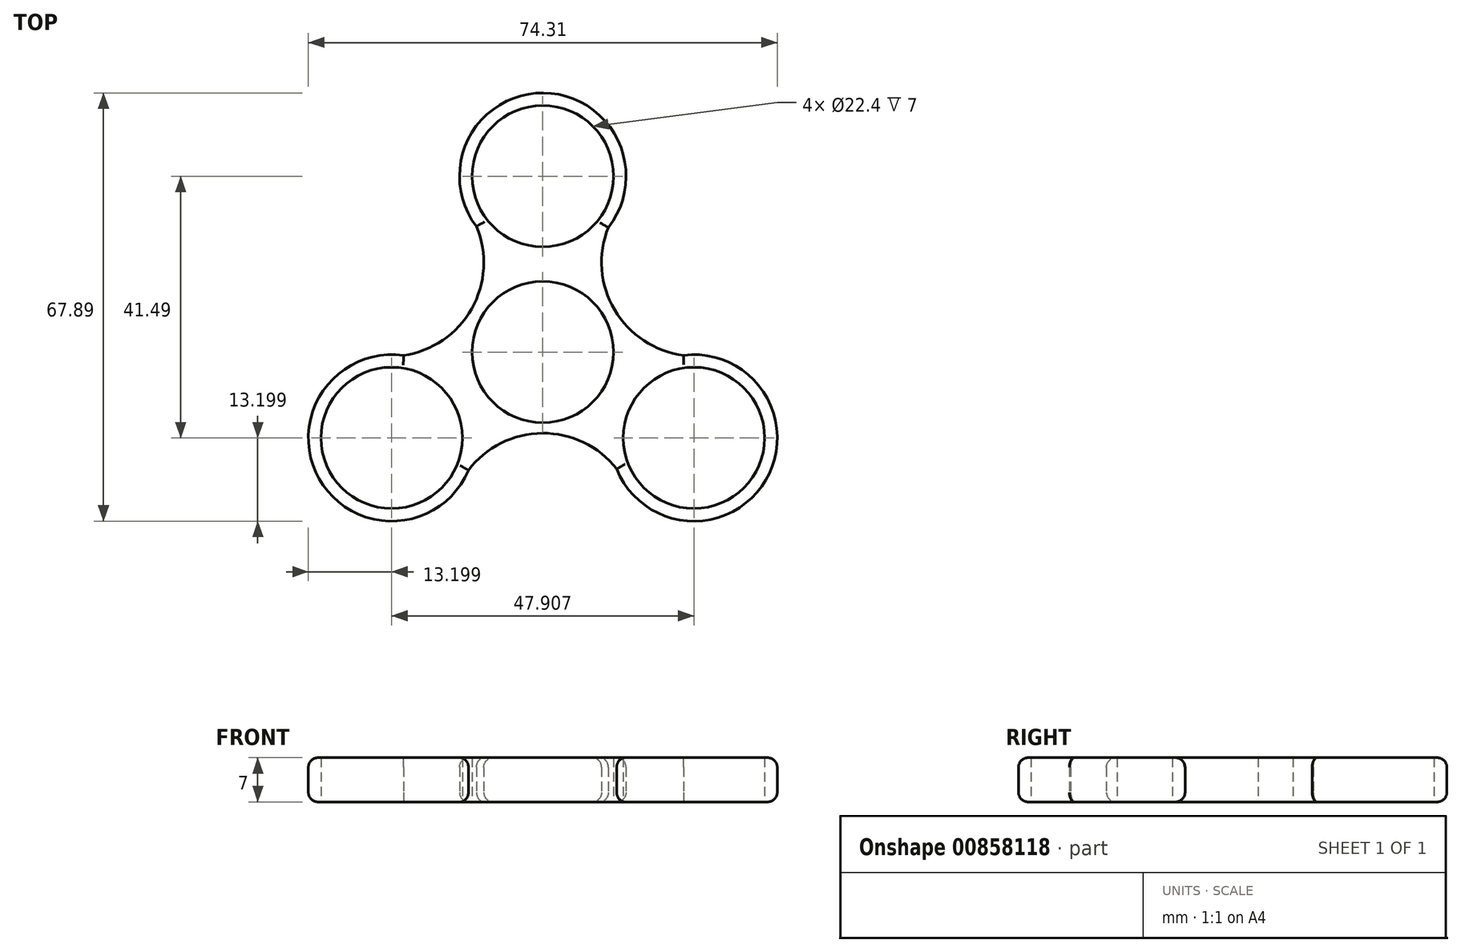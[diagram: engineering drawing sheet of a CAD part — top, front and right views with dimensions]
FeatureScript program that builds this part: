
annotation { "Feature Type Name" : "Feature", "Feature Type Description" : "" }
export const myFeature = defineFeature(function(context is Context, id is Id, definition is map)
    precondition{}
    {
        {
            var Q0;
            Q0=qCreatedBy(makeId("Top.planeOp"),FACE);
            var sketch = newSketch(context, id + "F0", { "sketchPlane" : qUnion([Q0])});
            skCircle(sketch, "E0", {"center": v(0, 0) * mm, "radius": 11.2 * mm});
            skArc(sketch, "E1", {"start": v(-2.14, -13.03) * mm, "mid": v(0.02, -13.2) * mm, "end": v(2.17, -13.02) * mm});
            skCircle(sketch, "E2", {"center": v(0, 27.88) * mm, "radius": 11.2 * mm});
            skArc(sketch, "E3", {"start": v(10.39, 19.74) * mm, "mid": v(0.1, 41.08) * mm, "end": v(-10.52, 19.9) * mm});
            skArc(sketch, "E4.1.0", {"start": v(-22.1, -0.54) * mm, "mid": v(-35.44, -20.12) * mm, "end": v(-11.79, -18.74) * mm});
            skCircle(sketch, "E4.1.1", {"center": v(-23.95, -13.61) * mm, "radius": 11.2 * mm});
            skArc(sketch, "E4.2.0", {"start": v(11.7, -18.53) * mm, "mid": v(35.33, -20.3) * mm, "end": v(22.31, -0.51) * mm});
            skCircle(sketch, "E4.2.1", {"center": v(23.96, -13.6) * mm, "radius": 11.2 * mm});
            skPoint(sketch, "E4.center", {"position": v(0, 0.22) * mm});
            skArc(sketch, "E5", {"start": v(10.39, 19.74) * mm, "mid": v(11.38, 6.68) * mm, "end": v(22.31, -0.51) * mm});
            skArc(sketch, "E6.1.0", {"start": v(-22.1, -0.54) * mm, "mid": v(-11.29, 6.84) * mm, "end": v(-10.52, 19.9) * mm});
            skArc(sketch, "E6.2.0", {"start": v(11.7, -18.53) * mm, "mid": v(-0.09, -12.87) * mm, "end": v(-11.79, -18.74) * mm});
            skArc(sketch, "E7.trimOffspring", {"start": v(-11.26, 6.89) * mm, "mid": v(-11.4, 6.66) * mm, "end": v(-11.53, 6.44) * mm});
            skLineSegment(sketch, "E8.trimOffspring", {"start": v(11.45, 6.57) * mm, "end": v(11.45, 6.57) * mm});
            skSolve(sketch);
        }
        {
            var Q0;
            Q0=makeQuery(id+"F0.imprint","IMPRINT",FACE,{"disambiguationData":[TD([[makeQuery(id+"F0.imprint","IMPRINT",EDGE,{"derivedFrom":sQuery(id+"F0.wireOp",EDGE,"E0")}),-1.0]])]});
            extrude(context, id + "F1", {"entities" : qUnion([Q0]), "depth" : 7 * mm, "offsetDistance" : 25 * mm});
        }
        {
            var Q0;
            Q0=makeQuery(id+"F1.opExtrude","CAP_EDGE",EDGE,{"disambiguationData":[OSD([sQuery(id+"F0.wireOp",EDGE,"E4.1.0")])],"isStart":false});
            var Q1;
            Q1=makeQuery(id+"F1.opExtrude","CAP_EDGE",EDGE,{"disambiguationData":[OSD([sQuery(id+"F0.wireOp",EDGE,"E6.1.0")])],"isStart":false});
            var Q2;
            Q2=makeQuery(id+"F1.opExtrude","CAP_EDGE",EDGE,{"disambiguationData":[OSD([sQuery(id+"F0.wireOp",EDGE,"E3")])],"isStart":false});
            var Q3;
            Q3=makeQuery(id+"F1.opExtrude","CAP_EDGE",EDGE,{"disambiguationData":[OSD([sQuery(id+"F0.wireOp",EDGE,"E6.2.0")])],"isStart":false});
            var Q4;
            Q4=makeQuery(id+"F1.opExtrude","CAP_EDGE",EDGE,{"disambiguationData":[OSD([sQuery(id+"F0.wireOp",EDGE,"E4.2.0")])],"isStart":false});
            var Q5;
            Q5=makeQuery(id+"F1.opExtrude","CAP_EDGE",EDGE,{"disambiguationData":[OSD([sQuery(id+"F0.wireOp",EDGE,"E5")])],"isStart":false});
            fillet(context, id + "F2", {"entities" : qUnion([Q0, Q1, Q2, Q3, Q4, Q5]), "radius" : 1.5 * mm, "tangentPropagation" : true, "allowEdgeOverflow" : false});
        }
        {
            var Q0;
            Q0=makeQuery(id+"F1.opExtrude","CAP_EDGE",EDGE,{"disambiguationData":[OSD([sQuery(id+"F0.wireOp",EDGE,"E4.2.0")])],"isStart":true});
            var Q1;
            Q1=makeQuery(id+"F1.opExtrude","CAP_EDGE",EDGE,{"disambiguationData":[OSD([sQuery(id+"F0.wireOp",EDGE,"E5")])],"isStart":true});
            var Q2;
            Q2=makeQuery(id+"F1.opExtrude","CAP_EDGE",EDGE,{"disambiguationData":[OSD([sQuery(id+"F0.wireOp",EDGE,"E3")])],"isStart":true});
            var Q3;
            Q3=makeQuery(id+"F1.opExtrude","CAP_EDGE",EDGE,{"disambiguationData":[OSD([sQuery(id+"F0.wireOp",EDGE,"E6.1.0")])],"isStart":true});
            var Q4;
            Q4=makeQuery(id+"F1.opExtrude","CAP_EDGE",EDGE,{"disambiguationData":[OSD([sQuery(id+"F0.wireOp",EDGE,"E4.1.0")])],"isStart":true});
            var Q5;
            Q5=makeQuery(id+"F1.opExtrude","CAP_EDGE",EDGE,{"disambiguationData":[OSD([sQuery(id+"F0.wireOp",EDGE,"E6.2.0")])],"isStart":true});
            fillet(context, id + "F3", {"entities" : qUnion([Q0, Q1, Q2, Q3, Q4, Q5]), "radius" : 1.5 * mm, "tangentPropagation" : true, "allowEdgeOverflow" : false});
        }
    });
